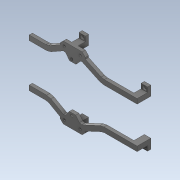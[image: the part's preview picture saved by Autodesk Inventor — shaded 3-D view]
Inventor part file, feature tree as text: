
AUTODESK INVENTOR PART (.ipt)
format: ipt  version: 2020 (Build 240168000, 168)  size: 717,312 bytes
history: native  units: mm
features: projected_geometry x29, extrude x14, sketch x13, chamfer x6, other x5, reference x3
ambient origin geometry x8: Origin, YZ Plane, XZ Plane, XY Plane, X Axis, Y Axis, Z Axis, Center Point
bodies: Solid1 (feature_tree)
feature tree (70):
  extrude  "Extrusion1"  Depth=8.0mm
  extrude  "Extrusion2"  Depth=8.0mm
  extrude  "Extrusion3"  Depth=12.0mm
  extrude  "Extrusion4"  Depth=6.0mm
  extrude  "Extrusion5"  Depth=6.0mm
  extrude  "Extrusion6"  Depth=9.0mm TaperAngle=0.0deg
  chamfer  "Chamfer2"  Distance=30.0mm
  extrude  "Extrusion12"  Depth=4.0mm TaperAngle=0.0deg
  chamfer  "Chamfer3"  Distance=5.6mm
  extrude  "Extrusion13"  Depth=6.0mm
  chamfer  "Chamfer4"  Distance=5.6mm
  chamfer  "Chamfer5"  Distance=5.6mm
  extrude  "Extrusion26"  Depth=6.0mm
  extrude  "Extrusion27"  Depth=4.0mm
  extrude  "Extrusion28"  Depth=6.0mm
  extrude  "Extrusion29"  Depth=4.0mm
  extrude  "Extrusion30"  Depth=6.0mm
  chamfer  "Chamfer9"  Distance=81.315041mm
  extrude  "Extrusion31"  Depth=6.0mm
  chamfer  "Chamfer11"  Distance=81.315041mm
  sketch  "Sketch1"  dims[d0=8.0mm d1=20.200077mm]
  reference  "Reference1"
  sketch  "Sketch2"  dims[d2=12.0mm d3=8.0mm]
  projected_geometry  "Projected Loop1"
  projected_geometry  "Projected Loop2"
  projected_geometry  "Projected Loop3"
  projected_geometry  "Projected Loop4"
  sketch  "Sketch3"  dims[d4=12.0mm d5=4.215041mm]
  projected_geometry  "Projected Loop5"
  projected_geometry  "Projected Loop6"
  projected_geometry  "Projected Loop7"
  projected_geometry  "Projected Loop8"
  sketch  "Sketch4"  dims[d6=4.0mm d7=0.0mm d8=6.0mm]
  projected_geometry  "Projected Loop9"
  projected_geometry  "Projected Loop10"
  projected_geometry  "Projected Loop11"
  projected_geometry  "Projected Loop12"
  sketch  "Sketch5"  dims[d9=6.0mm d10=6.0mm]
  projected_geometry  "Projected Loop13"
  projected_geometry  "Projected Loop14"
  projected_geometry  "Projected Loop15"
  projected_geometry  "Projected Loop16"
  sketch  "Sketch6"  dims[d11=6.0mm d12=9.0mm d13=0.0mm]
  projected_geometry  "Projected Loop17"
  projected_geometry  "Projected Loop18"
  projected_geometry  "Projected Loop19"
  sketch  "Sketch13"  dims[d14=11.34464mm]
  projected_geometry  "Projected Loop28"
  projected_geometry  "Projected Loop29"
  projected_geometry  "Projected Loop30"
  sketch  "Sketch14"  dims[d15=11.34464mm]
  projected_geometry  "Projected Loop31"
  sketch  "Sketch27"  dims[d16=10.559242mm]
  reference  "Reference2"
  reference  "Reference3"
  sketch  "Sketch28"  dims[d17=10.559242mm]
  projected_geometry  "Projected Loop45"
  sketch  "Sketch29"  dims[d18=20.856685mm]
  projected_geometry  "Projected Loop46"
  sketch  "Sketch30"  dims[d19=20.856685mm]
  projected_geometry  "Projected Loop47"
  projected_geometry  "Projected Loop48"
  projected_geometry  "Projected Loop49"
  sketch  "Sketch31"  dims[d20=60.0mm d21=30.0mm d22=4.0mm d23=0.0mm d24=5.6mm d25=5.6mm d26=5.6mm d27=5.6mm d28=3.0mm d29=4.0mm d30=66.2mm d31=4.0mm d32=13.100038mm d33=81.315041mm d34=82.300038mm d35=81.315041mm d36=2.4mm d37=0.0mm d38=3.0mm d39=3.0mm d40=3.0mm d41=3.0mm d42=2.0mm d43=0.0mm d44=26.0mm d45=0.0mm d100=2.0mm d101=2.0mm d102=45.0deg d105=65.6mm d106=4.0mm d107=0.0mm d108=56.0mm d109=47.6mm d110=4.8mm d111=57.2mm d112=4.8mm d113=65.6mm d114=19.0mm d115=2.5mm d116=2.5mm d117=2.5mm d118=2.0mm d119=2.0mm d120=45.0deg d121=10.0mm d122=20.0mm d123=10.0mm d124=2.5mm d125=2.5mm d126=20.0mm d127=4.0mm d128=0.0mm d129=2.0mm d130=2.0mm d131=45.0deg d132=2.0mm d133=2.0mm d134=45.0deg d197=10.0mm d198=0.0mm d199=26.0mm d200=0.0mm d201=1.0mm d205=7.0mm d206=1.0mm d207=7.0mm d208=2.4mm d209=0.0mm d210=3.0mm d211=3.0mm d212=2.4mm d213=0.0mm d214=45.0mm d215=100.0mm d216=0.0mm d220=4.0mm d221=2.0mm d222=45.0deg d223=6.0mm d224=21.0mm d225=6.0mm d226=21.0mm d227=21.0mm d228=10.0mm d229=0.0mm d233=6.0mm d234=3.0mm d235=5.0mm d236=3.0mm d237=2.0mm d238=2.0mm d239=45.0deg d240=3.0mm d241=3.0mm d69=0.5mm d70=0.872665mm d71=0.5mm d72=0.872665mm]
  projected_geometry  "Projected Loop50"
  parser-record x2  (decoder bookkeeping rows leaked as tree rows — omitted from the tree; the rows remain in map.json)
  other  "Assembly1.iam"
  other  "BodyBot:1"
  other  "Hexa:1"
note: 2 file-system paths scrubbed to <path> (originals preserved in map.json)
